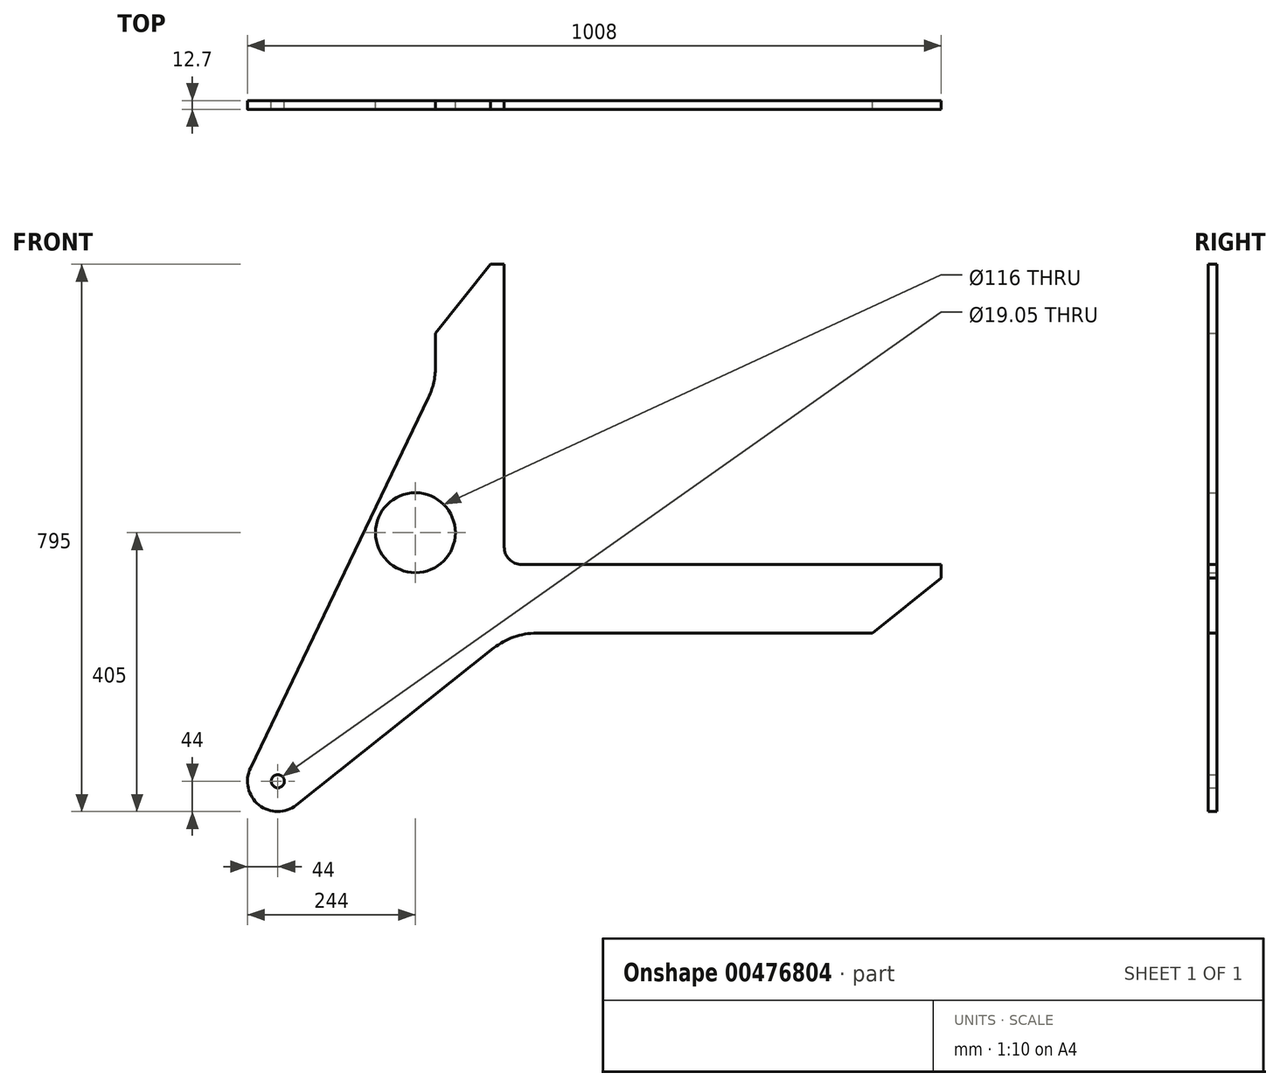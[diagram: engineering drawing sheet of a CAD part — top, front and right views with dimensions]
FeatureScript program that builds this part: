
annotation { "Feature Type Name" : "Feature", "Feature Type Description" : "" }
export const myFeature = defineFeature(function(context is Context, id is Id, definition is map)
    precondition{}
    {
        {
            var Q0;
            Q0=qCreatedBy(makeId("Front.planeOp"),FACE);
            var sketch = newSketch(context, id + "F0", { "sketchPlane" : qUnion([Q0])});
            skCircle(sketch, "E0", {"center": v(0, 0) * mm, "radius": 58 * mm});
            skCircle(sketch, "E1", {"center": v(-200, -361) * mm, "radius": 9.53 * mm});
            skArc(sketch, "E2", {"start": v(-239.66, -341.94) * mm, "mid": v(-227.44, -395.4) * mm, "end": v(-172.62, -395.44) * mm});
            skLineSegment(sketch, "E3", {"start": v(-172.62, -395.44) * mm, "end": v(113.76, -167.73) * mm});
            skLineSegment(sketch, "E4", {"start": v(176, -146) * mm, "end": v(664, -146) * mm});
            skLineSegment(sketch, "E5", {"start": v(664, -146) * mm, "end": v(764, -66) * mm});
            skLineSegment(sketch, "E6", {"start": v(764, -66) * mm, "end": v(764, -46) * mm});
            skLineSegment(sketch, "E7", {"start": v(764, -46) * mm, "end": v(154, -46) * mm});
            skLineSegment(sketch, "E8", {"start": v(129, -21) * mm, "end": v(129, 390) * mm});
            skLineSegment(sketch, "E9", {"start": v(129, 390) * mm, "end": v(109, 390) * mm});
            skLineSegment(sketch, "E10", {"start": v(109, 390) * mm, "end": v(29, 290) * mm});
            skLineSegment(sketch, "E11", {"start": v(29, 290) * mm, "end": v(29, 240) * mm});
            skLineSegment(sketch, "E12", {"start": v(19.14, 196.7) * mm, "end": v(-239.66, -341.94) * mm});
            skPoint(sketch, "E13.visualSharp", {"position": v(29, 217.22) * mm});
            skArc(sketch, "E13.filletArc", {"start": v(19.14, 196.7) * mm, "mid": v(26.5, 217.8) * mm, "end": v(29, 240) * mm});
            skPoint(sketch, "E14.visualSharp", {"position": v(141.09, -146) * mm});
            skArc(sketch, "E14.filletArc", {"start": v(176, -146) * mm, "mid": v(143.04, -151.59) * mm, "end": v(113.76, -167.73) * mm});
            skPoint(sketch, "E15.visualSharp", {"position": v(129, -46) * mm});
            skArc(sketch, "E15.filletArc", {"start": v(129, -21) * mm, "mid": v(136.32, -38.68) * mm, "end": v(154, -46) * mm});
            skSolve(sketch);
        }
        {
            var Q0;
            Q0=makeQuery(id+"F0.imprint","IMPRINT",FACE,{"disambiguationData":[TD([[makeQuery(id+"F0.imprint","IMPRINT",EDGE,{"derivedFrom":sQuery(id+"F0.wireOp",EDGE,"E0")}),-1.0]])]});
            extrude(context, id + "F1", {"entities" : qUnion([Q0]), "endBound" : BoundingType.SYMMETRIC, "depth" : (25.4 / 2) * mm});
        }
    });
